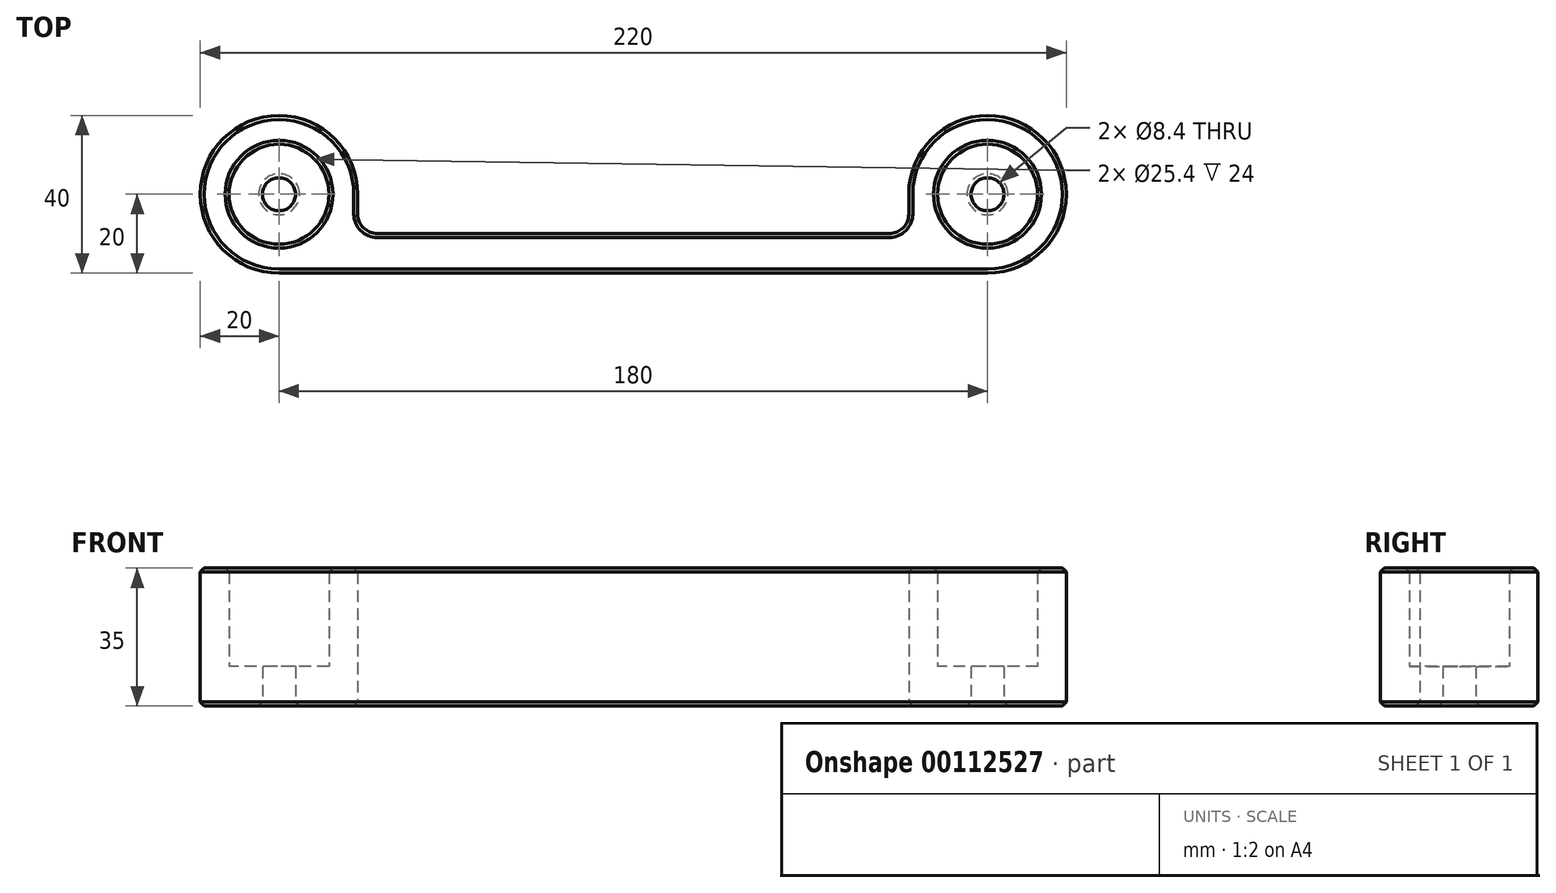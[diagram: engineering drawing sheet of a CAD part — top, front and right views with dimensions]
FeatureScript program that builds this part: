
annotation { "Feature Type Name" : "Feature", "Feature Type Description" : "" }
export const myFeature = defineFeature(function(context is Context, id is Id, definition is map)
    precondition{}
    {
        {
            var Q0;
            Q0=qCreatedBy(makeId("Top.planeOp"),FACE);
            var sketch = newSketch(context, id + "F0", { "sketchPlane" : qUnion([Q0])});
            skCircle(sketch, "E0", {"center": v(-90, 0) * mm, "radius": 4.2 * mm});
            skCircle(sketch, "E1", {"center": v(90, 0) * mm, "radius": 4.2 * mm});
            skArc(sketch, "E2", {"start": v(-70, 0) * mm, "mid": v(-104.14, 14.14) * mm, "end": v(-90, -20) * mm});
            skArc(sketch, "E3", {"start": v(90, -20) * mm, "mid": v(104.14, 14.14) * mm, "end": v(70, 0) * mm});
            skLineSegment(sketch, "E4", {"start": v(-90, -20) * mm, "end": v(90, -20) * mm});
            skLineSegment(sketch, "E5", {"start": v(-70, -10) * mm, "end": v(70, -10) * mm});
            skLineSegment(sketch, "E6", {"start": v(-70, 0) * mm, "end": v(-70, -10) * mm});
            skLineSegment(sketch, "E7", {"start": v(70, 0) * mm, "end": v(70, -10) * mm});
            skSolve(sketch);
        }
        {
            var Q0;
            Q0=makeQuery(id+"F0.imprint","IMPRINT",FACE,{"disambiguationData":[TD([[makeQuery(id+"F0.imprint","IMPRINT",EDGE,{"derivedFrom":sQuery(id+"F0.wireOp",EDGE,"E0")}),-1.0]])]});
            extrude(context, id + "F1", {"entities" : qUnion([Q0]), "depth" : 10 * mm});
        }
        {
            var Q0;
            Q0=makeQuery(id+"F1.opExtrude","CAP_FACE",FACE,{"disambiguationData":[OSD([sQuery(id+"F0.wireOp",EDGE,"E0"),sQuery(id+"F0.wireOp",EDGE,"E1"),sQuery(id+"F0.wireOp",EDGE,"E2"),sQuery(id+"F0.wireOp",EDGE,"E3"),sQuery(id+"F0.wireOp",EDGE,"E4"),sQuery(id+"F0.wireOp",EDGE,"E5"),sQuery(id+"F0.wireOp",EDGE,"E6"),sQuery(id+"F0.wireOp",EDGE,"E7")])],"isStart":false});
            var sketch = newSketch(context, id + "F2", { "sketchPlane" : qUnion([Q0])});
            skCircle(sketch, "E8", {"center": v(-90, 0) * mm, "radius": 12.7 * mm});
            skCircle(sketch, "E9", {"center": v(90, 0) * mm, "radius": 12.7 * mm});
            skSolve(sketch);
        }
        {
            var Q0;
            Q0=makeQuery(id+"F2.imprint","IMPRINT",FACE,{"disambiguationData":[TD([[makeQuery(id+"F2.imprint","IMPRINT",EDGE,{"derivedFrom":sQuery(id+"F2.wireOp",EDGE,"E8")}),-1.0]])]});
            extrude(context, id + "F3", {"entities" : qUnion([Q0]), "operationType" : NewBodyOperationType.ADD, "depth" : 25 * mm});
        }
        {
            var Q0;
            {var subQ0=sQuery(id+"F0.wireOp",EDGE,"E6");var subQ1=sQuery(id+"F0.wireOp",EDGE,"E5");Q0=makeQuery(id+"F3.boolean.opBoolean","MERGE",EDGE,{"derivedFrom":[makeQuery(id+"F1.opExtrude","SWEPT_EDGE",EDGE,{"disambiguationData":[OSD([subQ1,subQ0])]}),makeQuery(id+"F3.opExtrude","SWEPT_EDGE",EDGE,{"disambiguationData":[OSD([subQ1,subQ0])]})]});}
            var Q1;
            {var subQ0=sQuery(id+"F0.wireOp",EDGE,"E7");var subQ1=sQuery(id+"F0.wireOp",EDGE,"E5");Q1=makeQuery(id+"F3.boolean.opBoolean","MERGE",EDGE,{"derivedFrom":[makeQuery(id+"F1.opExtrude","SWEPT_EDGE",EDGE,{"disambiguationData":[OSD([subQ1,subQ0])]}),makeQuery(id+"F3.opExtrude","SWEPT_EDGE",EDGE,{"disambiguationData":[OSD([subQ1,subQ0])]})]});}
            fillet(context, id + "F4", {"entities" : qUnion([Q0, Q1]), "radius" : 5 * mm, "tangentPropagation" : true, "allowEdgeOverflow" : false});
        }
        {
            var Q0;
            Q0=makeQuery(id+"F1.opExtrude","CAP_FACE",FACE,{"disambiguationData":[OSD([sQuery(id+"F0.wireOp",EDGE,"E0"),sQuery(id+"F0.wireOp",EDGE,"E1"),sQuery(id+"F0.wireOp",EDGE,"E2"),sQuery(id+"F0.wireOp",EDGE,"E3"),sQuery(id+"F0.wireOp",EDGE,"E4"),sQuery(id+"F0.wireOp",EDGE,"E5"),sQuery(id+"F0.wireOp",EDGE,"E6"),sQuery(id+"F0.wireOp",EDGE,"E7")])],"isStart":true});
            var Q1;
            Q1=makeQuery(id+"F3.opExtrude","CAP_FACE",FACE,{"disambiguationData":[OSD([sQuery(id+"F0.wireOp",EDGE,"E2"),sQuery(id+"F0.wireOp",EDGE,"E3"),sQuery(id+"F0.wireOp",EDGE,"E4"),sQuery(id+"F0.wireOp",EDGE,"E5"),sQuery(id+"F0.wireOp",EDGE,"E6"),sQuery(id+"F0.wireOp",EDGE,"E7"),sQuery(id+"F2.wireOp",EDGE,"E8"),sQuery(id+"F2.wireOp",EDGE,"E9")])],"isStart":false});
            chamfer(context, id + "F5", {"entities" : qUnion([Q0, Q1]), "width" : 1 * mm, "tangentPropagation" : true});
        }
    });
